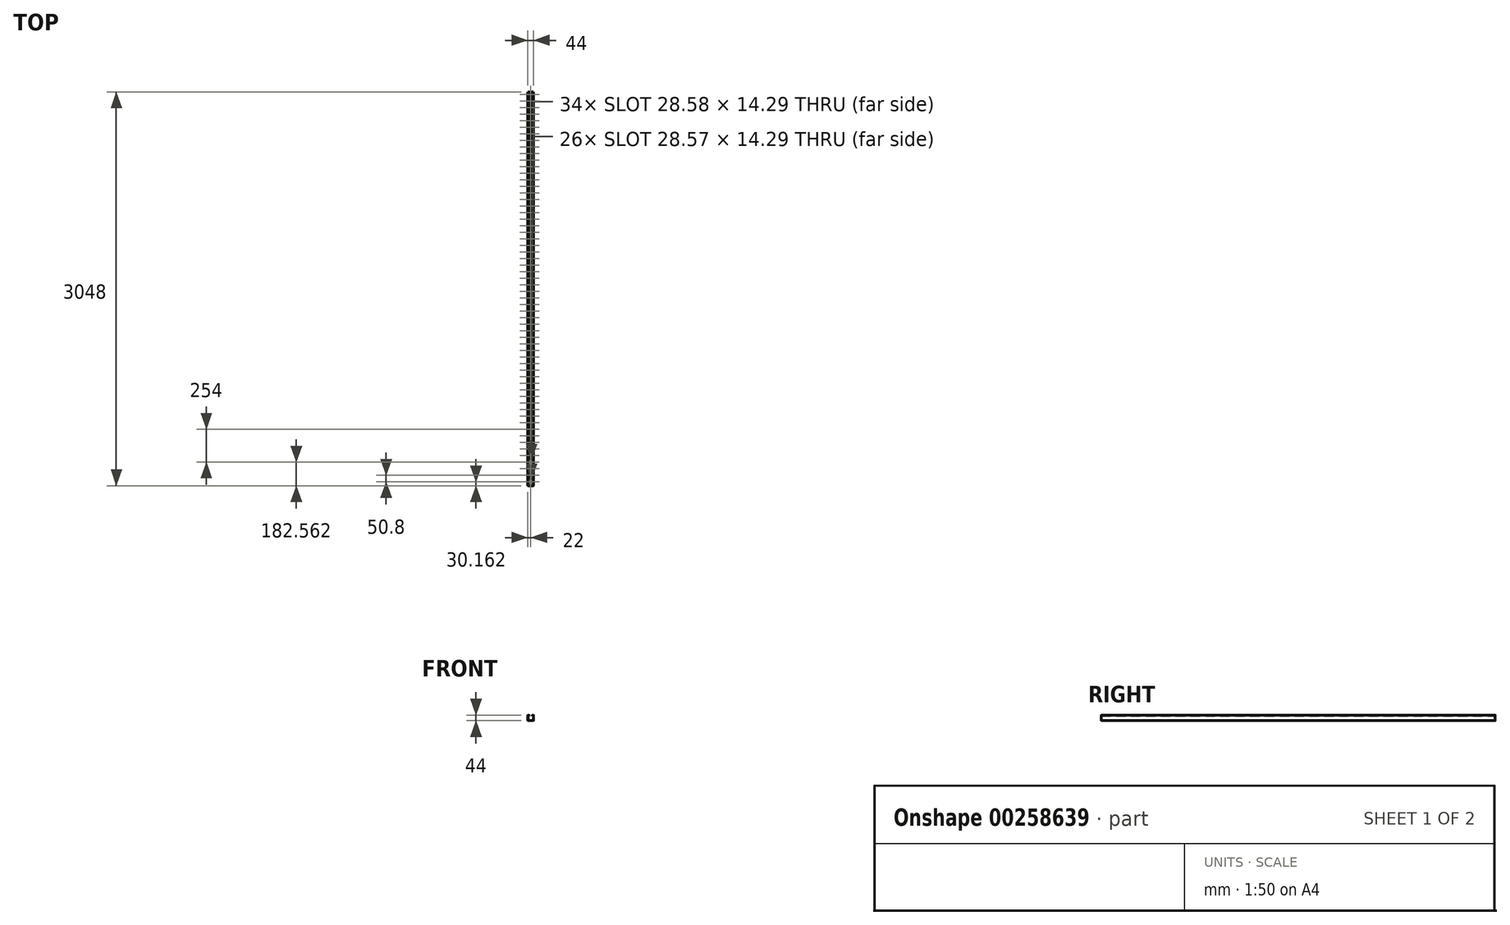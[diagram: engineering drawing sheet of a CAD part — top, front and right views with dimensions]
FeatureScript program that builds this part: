
annotation { "Feature Type Name" : "Feature", "Feature Type Description" : "" }
export const myFeature = defineFeature(function(context is Context, id is Id, definition is map)
    precondition{}
    {
        {
            var Q0;
            Q0=qCreatedBy(makeId("Front.planeOp"),FACE);
            var sketch = newSketch(context, id + "F0", { "sketchPlane" : qUnion([Q0])});
            skLineSegment(sketch, "E0.bottom", {"start": v(-22, 22) * mm, "end": v(22, 22) * mm, "construction": true});
            skLineSegment(sketch, "E0.top", {"start": v(-22, -22) * mm, "end": v(22, -22) * mm, "construction": true});
            skLineSegment(sketch, "E0.left", {"start": v(-22, 22) * mm, "end": v(-22, -22) * mm, "construction": true});
            skLineSegment(sketch, "E0.right", {"start": v(22, 22) * mm, "end": v(22, -22) * mm, "construction": true});
            skPoint(sketch, "E0.middle", {"position": v(0, 0) * mm});
            skLineSegment(sketch, "E1", {"start": v(0, -22) * mm, "end": v(-20.73, -22) * mm});
            skLineSegment(sketch, "E2", {"start": v(-20.73, 22) * mm, "end": v(-13.74, 22) * mm});
            skLineSegment(sketch, "E3", {"start": v(-12.47, 20.73) * mm, "end": v(-12.47, 14.85) * mm});
            skLineSegment(sketch, "E4", {"start": v(-22, -20.73) * mm, "end": v(-22, 20.73) * mm});
            skPoint(sketch, "E5.visualSharp", {"position": v(-22, -22) * mm});
            skArc(sketch, "E5.filletArc", {"start": v(-22, -20.73) * mm, "mid": v(-21.63, -21.63) * mm, "end": v(-20.73, -22) * mm});
            skPoint(sketch, "E6.visualSharp", {"position": v(-22, 22) * mm});
            skArc(sketch, "E6.filletArc", {"start": v(-20.73, 22) * mm, "mid": v(-21.63, 21.63) * mm, "end": v(-22, 20.73) * mm});
            skPoint(sketch, "E7.visualSharp", {"position": v(-12.47, 22) * mm});
            skArc(sketch, "E7.filletArc", {"start": v(-12.47, 20.73) * mm, "mid": v(-12.84, 21.63) * mm, "end": v(-13.74, 22) * mm});
            skLineSegment(sketch, "E8.0", {"start": v(-13.49, 20.73) * mm, "end": v(-13.49, 14.85) * mm});
            skArc(sketch, "E8.1", {"start": v(-13.49, 20.73) * mm, "mid": v(-13.56, 20.9) * mm, "end": v(-13.74, 20.98) * mm});
            skLineSegment(sketch, "E8.2", {"start": v(-20.73, 20.98) * mm, "end": v(-13.74, 20.98) * mm});
            skLineSegment(sketch, "E8.3", {"start": v(0, -20.98) * mm, "end": v(-20.73, -20.98) * mm});
            skArc(sketch, "E8.4", {"start": v(-20.98, -20.73) * mm, "mid": v(-20.9, -20.9) * mm, "end": v(-20.73, -20.98) * mm});
            skLineSegment(sketch, "E8.5", {"start": v(-20.98, -20.73) * mm, "end": v(-20.98, 20.73) * mm});
            skArc(sketch, "E8.6", {"start": v(-20.73, 20.98) * mm, "mid": v(-20.9, 20.9) * mm, "end": v(-20.98, 20.73) * mm});
            skLineSegment(sketch, "E9", {"start": v(-13.49, 14.85) * mm, "end": v(-12.47, 14.85) * mm});
            skLineSegment(sketch, "E10", {"start": v(0, -22) * mm, "end": v(0, -20.98) * mm});
            skSolve(sketch);
        }
        {
            var Q0;
            Q0 = qSketchRegion(id + "F0", true);
            extrude(context, id + "F1", {"entities" : qUnion([Q0]), "endBound" : BoundingType.SYMMETRIC, "depth" : 3048 * mm});
        }
        {
            var Q0;
            Q0=makeQuery(id+"F1.opExtrude","SWEPT_FACE",FACE,{"disambiguationData":[OSD([sQuery(id+"F0.wireOp",EDGE,"E8.3")])]});
            var sketch = newSketch(context, id + "F2", { "sketchPlane" : qUnion([Q0])});
            skLineSegment(sketch, "E11", {"start": v(-20.73, -1493.84) * mm, "end": v(41.03, -1493.84) * mm, "construction": true});
            skLineSegment(sketch, "E12.bottom", {"start": v(-7.14, -1479.55) * mm, "end": v(7.14, -1479.55) * mm, "construction": true});
            skLineSegment(sketch, "E12.top", {"start": v(-7.14, -1508.12) * mm, "end": v(7.14, -1508.12) * mm, "construction": true});
            skLineSegment(sketch, "E12.left", {"start": v(-7.14, -1479.55) * mm, "end": v(-7.14, -1508.12) * mm, "construction": true});
            skLineSegment(sketch, "E12.right", {"start": v(7.14, -1479.55) * mm, "end": v(7.14, -1508.12) * mm, "construction": true});
            skPoint(sketch, "E12.middle", {"position": v(0, -1493.84) * mm});
            skArc(sketch, "E13", {"start": v(0, -1479.55) * mm, "mid": v(-5.05, -1481.64) * mm, "end": v(-7.14, -1486.7) * mm});
            skArc(sketch, "E14", {"start": v(-7.14, -1500.98) * mm, "mid": v(-5.05, -1506.03) * mm, "end": v(0, -1508.12) * mm});
            skLineSegment(sketch, "E15", {"start": v(-7.14, -1486.7) * mm, "end": v(-7.14, -1500.98) * mm});
            skLineSegment(sketch, "E16", {"start": v(0, -1508.12) * mm, "end": v(0, -1479.55) * mm});
            skArc(sketch, "E17.0.1.0", {"start": v(0, -1428.75) * mm, "mid": v(-5.05, -1430.84) * mm, "end": v(-7.14, -1435.9) * mm});
            skLineSegment(sketch, "E17.0.1.1", {"start": v(0, -1457.33) * mm, "end": v(0, -1428.75) * mm});
            skArc(sketch, "E17.0.1.2", {"start": v(-7.14, -1450.18) * mm, "mid": v(-5.05, -1455.23) * mm, "end": v(0, -1457.33) * mm});
            skPoint(sketch, "E17.0.1.3", {"position": v(0, -1443.04) * mm});
            skLineSegment(sketch, "E17.0.1.4", {"start": v(7.14, -1428.75) * mm, "end": v(7.14, -1457.33) * mm, "construction": true});
            skLineSegment(sketch, "E17.0.1.5", {"start": v(-7.14, -1435.9) * mm, "end": v(-7.14, -1450.18) * mm});
            skArc(sketch, "E17.0.2.0", {"start": v(0, -1377.95) * mm, "mid": v(-5.05, -1380.04) * mm, "end": v(-7.14, -1385.1) * mm});
            skLineSegment(sketch, "E17.0.2.1", {"start": v(0, -1406.52) * mm, "end": v(0, -1377.95) * mm});
            skArc(sketch, "E17.0.2.2", {"start": v(-7.14, -1399.38) * mm, "mid": v(-5.05, -1404.43) * mm, "end": v(0, -1406.52) * mm});
            skPoint(sketch, "E17.0.2.3", {"position": v(0, -1392.24) * mm});
            skLineSegment(sketch, "E17.0.2.4", {"start": v(7.14, -1377.95) * mm, "end": v(7.14, -1406.52) * mm, "construction": true});
            skLineSegment(sketch, "E17.0.2.5", {"start": v(-7.14, -1385.1) * mm, "end": v(-7.14, -1399.38) * mm});
            skArc(sketch, "E17.0.3.0", {"start": v(0, -1327.15) * mm, "mid": v(-5.05, -1329.24) * mm, "end": v(-7.14, -1334.3) * mm});
            skLineSegment(sketch, "E17.0.3.1", {"start": v(0, -1355.72) * mm, "end": v(0, -1327.15) * mm});
            skArc(sketch, "E17.0.3.2", {"start": v(-7.14, -1348.58) * mm, "mid": v(-5.05, -1353.63) * mm, "end": v(0, -1355.72) * mm});
            skPoint(sketch, "E17.0.3.3", {"position": v(0, -1341.44) * mm});
            skLineSegment(sketch, "E17.0.3.4", {"start": v(7.14, -1327.15) * mm, "end": v(7.14, -1355.72) * mm, "construction": true});
            skLineSegment(sketch, "E17.0.3.5", {"start": v(-7.14, -1334.3) * mm, "end": v(-7.14, -1348.58) * mm});
            skArc(sketch, "E17.0.4.0", {"start": v(0, -1276.35) * mm, "mid": v(-5.05, -1278.44) * mm, "end": v(-7.14, -1283.5) * mm});
            skLineSegment(sketch, "E17.0.4.1", {"start": v(0, -1304.92) * mm, "end": v(0, -1276.35) * mm});
            skArc(sketch, "E17.0.4.2", {"start": v(-7.14, -1297.78) * mm, "mid": v(-5.05, -1302.83) * mm, "end": v(0, -1304.92) * mm});
            skPoint(sketch, "E17.0.4.3", {"position": v(0, -1290.64) * mm});
            skLineSegment(sketch, "E17.0.4.4", {"start": v(7.14, -1276.35) * mm, "end": v(7.14, -1304.92) * mm, "construction": true});
            skLineSegment(sketch, "E17.0.4.5", {"start": v(-7.14, -1283.5) * mm, "end": v(-7.14, -1297.78) * mm});
            skArc(sketch, "E17.0.5.0", {"start": v(0, -1225.55) * mm, "mid": v(-5.05, -1227.64) * mm, "end": v(-7.14, -1232.7) * mm});
            skLineSegment(sketch, "E17.0.5.1", {"start": v(0, -1254.12) * mm, "end": v(0, -1225.55) * mm});
            skArc(sketch, "E17.0.5.2", {"start": v(-7.14, -1246.98) * mm, "mid": v(-5.05, -1252.03) * mm, "end": v(0, -1254.12) * mm});
            skPoint(sketch, "E17.0.5.3", {"position": v(0, -1239.84) * mm});
            skLineSegment(sketch, "E17.0.5.4", {"start": v(7.14, -1225.55) * mm, "end": v(7.14, -1254.12) * mm, "construction": true});
            skLineSegment(sketch, "E17.0.5.5", {"start": v(-7.14, -1232.7) * mm, "end": v(-7.14, -1246.98) * mm});
            skArc(sketch, "E17.0.6.0", {"start": v(0, -1174.75) * mm, "mid": v(-5.05, -1176.84) * mm, "end": v(-7.14, -1181.9) * mm});
            skLineSegment(sketch, "E17.0.6.1", {"start": v(0, -1203.32) * mm, "end": v(0, -1174.75) * mm});
            skArc(sketch, "E17.0.6.2", {"start": v(-7.14, -1196.18) * mm, "mid": v(-5.05, -1201.23) * mm, "end": v(0, -1203.32) * mm});
            skPoint(sketch, "E17.0.6.3", {"position": v(0, -1189.04) * mm});
            skLineSegment(sketch, "E17.0.6.4", {"start": v(7.14, -1174.75) * mm, "end": v(7.14, -1203.32) * mm, "construction": true});
            skLineSegment(sketch, "E17.0.6.5", {"start": v(-7.14, -1181.9) * mm, "end": v(-7.14, -1196.18) * mm});
            skArc(sketch, "E17.0.7.0", {"start": v(0, -1123.95) * mm, "mid": v(-5.05, -1126.04) * mm, "end": v(-7.14, -1131.1) * mm});
            skLineSegment(sketch, "E17.0.7.1", {"start": v(0, -1152.52) * mm, "end": v(0, -1123.95) * mm});
            skArc(sketch, "E17.0.7.2", {"start": v(-7.14, -1145.38) * mm, "mid": v(-5.05, -1150.43) * mm, "end": v(0, -1152.52) * mm});
            skPoint(sketch, "E17.0.7.3", {"position": v(0, -1138.24) * mm});
            skLineSegment(sketch, "E17.0.7.4", {"start": v(7.14, -1123.95) * mm, "end": v(7.14, -1152.52) * mm, "construction": true});
            skLineSegment(sketch, "E17.0.7.5", {"start": v(-7.14, -1131.1) * mm, "end": v(-7.14, -1145.38) * mm});
            skArc(sketch, "E17.0.8.0", {"start": v(0, -1073.15) * mm, "mid": v(-5.05, -1075.24) * mm, "end": v(-7.14, -1080.3) * mm});
            skLineSegment(sketch, "E17.0.8.1", {"start": v(0, -1101.72) * mm, "end": v(0, -1073.15) * mm});
            skArc(sketch, "E17.0.8.2", {"start": v(-7.14, -1094.58) * mm, "mid": v(-5.05, -1099.63) * mm, "end": v(0, -1101.72) * mm});
            skPoint(sketch, "E17.0.8.3", {"position": v(0, -1087.44) * mm});
            skLineSegment(sketch, "E17.0.8.4", {"start": v(7.14, -1073.15) * mm, "end": v(7.14, -1101.72) * mm, "construction": true});
            skLineSegment(sketch, "E17.0.8.5", {"start": v(-7.14, -1080.3) * mm, "end": v(-7.14, -1094.58) * mm});
            skArc(sketch, "E17.0.9.0", {"start": v(0, -1022.35) * mm, "mid": v(-5.05, -1024.44) * mm, "end": v(-7.14, -1029.5) * mm});
            skLineSegment(sketch, "E17.0.9.1", {"start": v(0, -1050.92) * mm, "end": v(0, -1022.35) * mm});
            skArc(sketch, "E17.0.9.2", {"start": v(-7.14, -1043.78) * mm, "mid": v(-5.05, -1048.83) * mm, "end": v(0, -1050.92) * mm});
            skPoint(sketch, "E17.0.9.3", {"position": v(0, -1036.64) * mm});
            skLineSegment(sketch, "E17.0.9.4", {"start": v(7.14, -1022.35) * mm, "end": v(7.14, -1050.92) * mm, "construction": true});
            skLineSegment(sketch, "E17.0.9.5", {"start": v(-7.14, -1029.5) * mm, "end": v(-7.14, -1043.78) * mm});
            skArc(sketch, "E17.0.10.0", {"start": v(0, -971.55) * mm, "mid": v(-5.05, -973.64) * mm, "end": v(-7.14, -978.7) * mm});
            skLineSegment(sketch, "E17.0.10.1", {"start": v(0, -1000.12) * mm, "end": v(0, -971.55) * mm});
            skArc(sketch, "E17.0.10.2", {"start": v(-7.14, -992.98) * mm, "mid": v(-5.05, -998.03) * mm, "end": v(0, -1000.12) * mm});
            skPoint(sketch, "E17.0.10.3", {"position": v(0, -985.84) * mm});
            skLineSegment(sketch, "E17.0.10.4", {"start": v(7.14, -971.55) * mm, "end": v(7.14, -1000.12) * mm, "construction": true});
            skLineSegment(sketch, "E17.0.10.5", {"start": v(-7.14, -978.7) * mm, "end": v(-7.14, -992.98) * mm});
            skArc(sketch, "E17.0.11.0", {"start": v(0, -920.75) * mm, "mid": v(-5.05, -922.84) * mm, "end": v(-7.14, -927.9) * mm});
            skLineSegment(sketch, "E17.0.11.1", {"start": v(0, -949.32) * mm, "end": v(0, -920.75) * mm});
            skArc(sketch, "E17.0.11.2", {"start": v(-7.14, -942.18) * mm, "mid": v(-5.05, -947.23) * mm, "end": v(0, -949.32) * mm});
            skPoint(sketch, "E17.0.11.3", {"position": v(0, -935.04) * mm});
            skLineSegment(sketch, "E17.0.11.4", {"start": v(7.14, -920.75) * mm, "end": v(7.14, -949.32) * mm, "construction": true});
            skLineSegment(sketch, "E17.0.11.5", {"start": v(-7.14, -927.9) * mm, "end": v(-7.14, -942.18) * mm});
            skArc(sketch, "E17.0.12.0", {"start": v(0, -869.95) * mm, "mid": v(-5.05, -872.04) * mm, "end": v(-7.14, -877.1) * mm});
            skLineSegment(sketch, "E17.0.12.1", {"start": v(0, -898.52) * mm, "end": v(0, -869.95) * mm});
            skArc(sketch, "E17.0.12.2", {"start": v(-7.14, -891.38) * mm, "mid": v(-5.05, -896.43) * mm, "end": v(0, -898.52) * mm});
            skPoint(sketch, "E17.0.12.3", {"position": v(0, -884.24) * mm});
            skLineSegment(sketch, "E17.0.12.4", {"start": v(7.14, -869.95) * mm, "end": v(7.14, -898.52) * mm, "construction": true});
            skLineSegment(sketch, "E17.0.12.5", {"start": v(-7.14, -877.1) * mm, "end": v(-7.14, -891.38) * mm});
            skArc(sketch, "E17.0.13.0", {"start": v(0, -819.15) * mm, "mid": v(-5.05, -821.24) * mm, "end": v(-7.14, -826.3) * mm});
            skLineSegment(sketch, "E17.0.13.1", {"start": v(0, -847.72) * mm, "end": v(0, -819.15) * mm});
            skArc(sketch, "E17.0.13.2", {"start": v(-7.14, -840.58) * mm, "mid": v(-5.05, -845.63) * mm, "end": v(0, -847.72) * mm});
            skPoint(sketch, "E17.0.13.3", {"position": v(0, -833.44) * mm});
            skLineSegment(sketch, "E17.0.13.4", {"start": v(7.14, -819.15) * mm, "end": v(7.14, -847.72) * mm, "construction": true});
            skLineSegment(sketch, "E17.0.13.5", {"start": v(-7.14, -826.3) * mm, "end": v(-7.14, -840.58) * mm});
            skArc(sketch, "E17.0.14.0", {"start": v(0, -768.35) * mm, "mid": v(-5.05, -770.44) * mm, "end": v(-7.14, -775.5) * mm});
            skLineSegment(sketch, "E17.0.14.1", {"start": v(0, -796.92) * mm, "end": v(0, -768.35) * mm});
            skArc(sketch, "E17.0.14.2", {"start": v(-7.14, -789.78) * mm, "mid": v(-5.05, -794.83) * mm, "end": v(0, -796.92) * mm});
            skPoint(sketch, "E17.0.14.3", {"position": v(0, -782.64) * mm});
            skLineSegment(sketch, "E17.0.14.4", {"start": v(7.14, -768.35) * mm, "end": v(7.14, -796.92) * mm, "construction": true});
            skLineSegment(sketch, "E17.0.14.5", {"start": v(-7.14, -775.5) * mm, "end": v(-7.14, -789.78) * mm});
            skArc(sketch, "E17.0.15.0", {"start": v(0, -717.55) * mm, "mid": v(-5.05, -719.64) * mm, "end": v(-7.14, -724.7) * mm});
            skLineSegment(sketch, "E17.0.15.1", {"start": v(0, -746.12) * mm, "end": v(0, -717.55) * mm});
            skArc(sketch, "E17.0.15.2", {"start": v(-7.14, -738.98) * mm, "mid": v(-5.05, -744.03) * mm, "end": v(0, -746.12) * mm});
            skPoint(sketch, "E17.0.15.3", {"position": v(0, -731.84) * mm});
            skLineSegment(sketch, "E17.0.15.4", {"start": v(7.14, -717.55) * mm, "end": v(7.14, -746.12) * mm, "construction": true});
            skLineSegment(sketch, "E17.0.15.5", {"start": v(-7.14, -724.7) * mm, "end": v(-7.14, -738.98) * mm});
            skArc(sketch, "E17.0.16.0", {"start": v(0, -666.75) * mm, "mid": v(-5.05, -668.84) * mm, "end": v(-7.14, -673.9) * mm});
            skLineSegment(sketch, "E17.0.16.1", {"start": v(0, -695.32) * mm, "end": v(0, -666.75) * mm});
            skArc(sketch, "E17.0.16.2", {"start": v(-7.14, -688.18) * mm, "mid": v(-5.05, -693.23) * mm, "end": v(0, -695.32) * mm});
            skPoint(sketch, "E17.0.16.3", {"position": v(0, -681.04) * mm});
            skLineSegment(sketch, "E17.0.16.4", {"start": v(7.14, -666.75) * mm, "end": v(7.14, -695.32) * mm, "construction": true});
            skLineSegment(sketch, "E17.0.16.5", {"start": v(-7.14, -673.9) * mm, "end": v(-7.14, -688.18) * mm});
            skArc(sketch, "E17.0.17.0", {"start": v(0, -615.95) * mm, "mid": v(-5.05, -618.04) * mm, "end": v(-7.14, -623.1) * mm});
            skLineSegment(sketch, "E17.0.17.1", {"start": v(0, -644.52) * mm, "end": v(0, -615.95) * mm});
            skArc(sketch, "E17.0.17.2", {"start": v(-7.14, -637.38) * mm, "mid": v(-5.05, -642.43) * mm, "end": v(0, -644.52) * mm});
            skPoint(sketch, "E17.0.17.3", {"position": v(0, -630.24) * mm});
            skLineSegment(sketch, "E17.0.17.4", {"start": v(7.14, -615.95) * mm, "end": v(7.14, -644.52) * mm, "construction": true});
            skLineSegment(sketch, "E17.0.17.5", {"start": v(-7.14, -623.1) * mm, "end": v(-7.14, -637.38) * mm});
            skArc(sketch, "E17.0.18.0", {"start": v(0, -565.15) * mm, "mid": v(-5.05, -567.24) * mm, "end": v(-7.14, -572.3) * mm});
            skLineSegment(sketch, "E17.0.18.1", {"start": v(0, -593.72) * mm, "end": v(0, -565.15) * mm});
            skArc(sketch, "E17.0.18.2", {"start": v(-7.14, -586.58) * mm, "mid": v(-5.05, -591.63) * mm, "end": v(0, -593.72) * mm});
            skPoint(sketch, "E17.0.18.3", {"position": v(0, -579.44) * mm});
            skLineSegment(sketch, "E17.0.18.4", {"start": v(7.14, -565.15) * mm, "end": v(7.14, -593.72) * mm, "construction": true});
            skLineSegment(sketch, "E17.0.18.5", {"start": v(-7.14, -572.3) * mm, "end": v(-7.14, -586.58) * mm});
            skArc(sketch, "E17.0.19.0", {"start": v(0, -514.35) * mm, "mid": v(-5.05, -516.44) * mm, "end": v(-7.14, -521.5) * mm});
            skLineSegment(sketch, "E17.0.19.1", {"start": v(0, -542.92) * mm, "end": v(0, -514.35) * mm});
            skArc(sketch, "E17.0.19.2", {"start": v(-7.14, -535.78) * mm, "mid": v(-5.05, -540.83) * mm, "end": v(0, -542.92) * mm});
            skPoint(sketch, "E17.0.19.3", {"position": v(0, -528.64) * mm});
            skLineSegment(sketch, "E17.0.19.4", {"start": v(7.14, -514.35) * mm, "end": v(7.14, -542.92) * mm, "construction": true});
            skLineSegment(sketch, "E17.0.19.5", {"start": v(-7.14, -521.5) * mm, "end": v(-7.14, -535.78) * mm});
            skArc(sketch, "E17.0.20.0", {"start": v(0, -463.55) * mm, "mid": v(-5.05, -465.64) * mm, "end": v(-7.14, -470.7) * mm});
            skLineSegment(sketch, "E17.0.20.1", {"start": v(0, -492.12) * mm, "end": v(0, -463.55) * mm});
            skArc(sketch, "E17.0.20.2", {"start": v(-7.14, -484.98) * mm, "mid": v(-5.05, -490.03) * mm, "end": v(0, -492.12) * mm});
            skPoint(sketch, "E17.0.20.3", {"position": v(0, -477.84) * mm});
            skLineSegment(sketch, "E17.0.20.4", {"start": v(7.14, -463.55) * mm, "end": v(7.14, -492.12) * mm, "construction": true});
            skLineSegment(sketch, "E17.0.20.5", {"start": v(-7.14, -470.7) * mm, "end": v(-7.14, -484.98) * mm});
            skArc(sketch, "E17.0.21.0", {"start": v(0, -412.75) * mm, "mid": v(-5.05, -414.84) * mm, "end": v(-7.14, -419.9) * mm});
            skLineSegment(sketch, "E17.0.21.1", {"start": v(0, -441.32) * mm, "end": v(0, -412.75) * mm});
            skArc(sketch, "E17.0.21.2", {"start": v(-7.14, -434.18) * mm, "mid": v(-5.05, -439.23) * mm, "end": v(0, -441.32) * mm});
            skPoint(sketch, "E17.0.21.3", {"position": v(0, -427.04) * mm});
            skLineSegment(sketch, "E17.0.21.4", {"start": v(7.14, -412.75) * mm, "end": v(7.14, -441.32) * mm, "construction": true});
            skLineSegment(sketch, "E17.0.21.5", {"start": v(-7.14, -419.9) * mm, "end": v(-7.14, -434.18) * mm});
            skArc(sketch, "E17.0.22.0", {"start": v(0, -361.95) * mm, "mid": v(-5.05, -364.04) * mm, "end": v(-7.14, -369.1) * mm});
            skLineSegment(sketch, "E17.0.22.1", {"start": v(0, -390.52) * mm, "end": v(0, -361.95) * mm});
            skArc(sketch, "E17.0.22.2", {"start": v(-7.14, -383.38) * mm, "mid": v(-5.05, -388.43) * mm, "end": v(0, -390.52) * mm});
            skPoint(sketch, "E17.0.22.3", {"position": v(0, -376.24) * mm});
            skLineSegment(sketch, "E17.0.22.4", {"start": v(7.14, -361.95) * mm, "end": v(7.14, -390.52) * mm, "construction": true});
            skLineSegment(sketch, "E17.0.22.5", {"start": v(-7.14, -369.1) * mm, "end": v(-7.14, -383.38) * mm});
            skArc(sketch, "E17.0.23.0", {"start": v(0, -311.15) * mm, "mid": v(-5.05, -313.24) * mm, "end": v(-7.14, -318.3) * mm});
            skLineSegment(sketch, "E17.0.23.1", {"start": v(0, -339.72) * mm, "end": v(0, -311.15) * mm});
            skArc(sketch, "E17.0.23.2", {"start": v(-7.14, -332.58) * mm, "mid": v(-5.05, -337.63) * mm, "end": v(0, -339.72) * mm});
            skPoint(sketch, "E17.0.23.3", {"position": v(0, -325.44) * mm});
            skLineSegment(sketch, "E17.0.23.4", {"start": v(7.14, -311.15) * mm, "end": v(7.14, -339.72) * mm, "construction": true});
            skLineSegment(sketch, "E17.0.23.5", {"start": v(-7.14, -318.3) * mm, "end": v(-7.14, -332.58) * mm});
            skArc(sketch, "E17.0.24.0", {"start": v(0, -260.35) * mm, "mid": v(-5.05, -262.44) * mm, "end": v(-7.14, -267.5) * mm});
            skLineSegment(sketch, "E17.0.24.1", {"start": v(0, -288.92) * mm, "end": v(0, -260.35) * mm});
            skArc(sketch, "E17.0.24.2", {"start": v(-7.14, -281.78) * mm, "mid": v(-5.05, -286.83) * mm, "end": v(0, -288.92) * mm});
            skPoint(sketch, "E17.0.24.3", {"position": v(0, -274.64) * mm});
            skLineSegment(sketch, "E17.0.24.4", {"start": v(7.14, -260.35) * mm, "end": v(7.14, -288.92) * mm, "construction": true});
            skLineSegment(sketch, "E17.0.24.5", {"start": v(-7.14, -267.5) * mm, "end": v(-7.14, -281.78) * mm});
            skLineSegment(sketch, "E17.direction1", {"start": v(0, -1508.12) * mm, "end": v(25.4, -1508.12) * mm, "construction": true});
            skLineSegment(sketch, "E17.direction2", {"start": v(0, -1508.12) * mm, "end": v(0, -1457.33) * mm, "construction": true});
            skArc(sketch, "E18.0.0.25", {"start": v(0, -209.55) * mm, "mid": v(-5.05, -211.64) * mm, "end": v(-7.14, -216.7) * mm});
            skLineSegment(sketch, "E18.4.0.25", {"start": v(0, -238.12) * mm, "end": v(0, -209.55) * mm});
            skArc(sketch, "E18.7.0.25", {"start": v(-7.14, -230.98) * mm, "mid": v(-5.05, -236.03) * mm, "end": v(0, -238.12) * mm});
            skPoint(sketch, "E18.11.0.25", {"position": v(0, -223.84) * mm});
            skLineSegment(sketch, "E18.12.0.25", {"start": v(7.14, -209.55) * mm, "end": v(7.14, -238.12) * mm, "construction": true});
            skLineSegment(sketch, "E18.15.0.25", {"start": v(-7.14, -216.7) * mm, "end": v(-7.14, -230.98) * mm});
            skArc(sketch, "E18.0.0.26", {"start": v(0, -158.75) * mm, "mid": v(-5.05, -160.84) * mm, "end": v(-7.14, -165.9) * mm});
            skLineSegment(sketch, "E18.4.0.26", {"start": v(0, -187.32) * mm, "end": v(0, -158.75) * mm});
            skArc(sketch, "E18.7.0.26", {"start": v(-7.14, -180.18) * mm, "mid": v(-5.05, -185.23) * mm, "end": v(0, -187.32) * mm});
            skPoint(sketch, "E18.11.0.26", {"position": v(0, -173.04) * mm});
            skLineSegment(sketch, "E18.12.0.26", {"start": v(7.14, -158.75) * mm, "end": v(7.14, -187.32) * mm, "construction": true});
            skLineSegment(sketch, "E18.15.0.26", {"start": v(-7.14, -165.9) * mm, "end": v(-7.14, -180.18) * mm});
            skArc(sketch, "E18.0.0.27", {"start": v(0, -107.95) * mm, "mid": v(-5.05, -110.04) * mm, "end": v(-7.14, -115.1) * mm});
            skLineSegment(sketch, "E18.4.0.27", {"start": v(0, -136.52) * mm, "end": v(0, -107.95) * mm});
            skArc(sketch, "E18.7.0.27", {"start": v(-7.14, -129.38) * mm, "mid": v(-5.05, -134.43) * mm, "end": v(0, -136.52) * mm});
            skPoint(sketch, "E18.11.0.27", {"position": v(0, -122.24) * mm});
            skLineSegment(sketch, "E18.12.0.27", {"start": v(7.14, -107.95) * mm, "end": v(7.14, -136.52) * mm, "construction": true});
            skLineSegment(sketch, "E18.15.0.27", {"start": v(-7.14, -115.1) * mm, "end": v(-7.14, -129.38) * mm});
            skArc(sketch, "E18.0.0.28", {"start": v(0, -57.15) * mm, "mid": v(-5.05, -59.24) * mm, "end": v(-7.14, -64.3) * mm});
            skLineSegment(sketch, "E18.4.0.28", {"start": v(0, -85.72) * mm, "end": v(0, -57.15) * mm});
            skArc(sketch, "E18.7.0.28", {"start": v(-7.14, -78.58) * mm, "mid": v(-5.05, -83.63) * mm, "end": v(0, -85.72) * mm});
            skPoint(sketch, "E18.11.0.28", {"position": v(0, -71.44) * mm});
            skLineSegment(sketch, "E18.12.0.28", {"start": v(7.14, -57.15) * mm, "end": v(7.14, -85.72) * mm, "construction": true});
            skLineSegment(sketch, "E18.15.0.28", {"start": v(-7.14, -64.3) * mm, "end": v(-7.14, -78.58) * mm});
            skArc(sketch, "E18.0.0.29", {"start": v(0, -6.35) * mm, "mid": v(-5.05, -8.44) * mm, "end": v(-7.14, -13.5) * mm});
            skLineSegment(sketch, "E18.4.0.29", {"start": v(0, -34.92) * mm, "end": v(0, -6.35) * mm});
            skArc(sketch, "E18.7.0.29", {"start": v(-7.14, -27.78) * mm, "mid": v(-5.05, -32.83) * mm, "end": v(0, -34.92) * mm});
            skPoint(sketch, "E18.11.0.29", {"position": v(0, -20.64) * mm});
            skLineSegment(sketch, "E18.12.0.29", {"start": v(7.14, -6.35) * mm, "end": v(7.14, -34.92) * mm, "construction": true});
            skLineSegment(sketch, "E18.15.0.29", {"start": v(-7.14, -13.5) * mm, "end": v(-7.14, -27.78) * mm});
            skArc(sketch, "E18.0.0.30", {"start": v(0, 44.45) * mm, "mid": v(-5.05, 42.36) * mm, "end": v(-7.14, 37.3) * mm});
            skLineSegment(sketch, "E18.4.0.30", {"start": v(0, 15.88) * mm, "end": v(0, 44.45) * mm});
            skArc(sketch, "E18.7.0.30", {"start": v(-7.14, 23.02) * mm, "mid": v(-5.05, 17.97) * mm, "end": v(0, 15.88) * mm});
            skPoint(sketch, "E18.11.0.30", {"position": v(0, 30.16) * mm});
            skLineSegment(sketch, "E18.12.0.30", {"start": v(7.14, 44.45) * mm, "end": v(7.14, 15.88) * mm, "construction": true});
            skLineSegment(sketch, "E18.15.0.30", {"start": v(-7.14, 37.3) * mm, "end": v(-7.14, 23.02) * mm});
            skArc(sketch, "E18.0.0.31", {"start": v(0, 95.25) * mm, "mid": v(-5.05, 93.16) * mm, "end": v(-7.14, 88.1) * mm});
            skLineSegment(sketch, "E18.4.0.31", {"start": v(0, 66.68) * mm, "end": v(0, 95.25) * mm});
            skArc(sketch, "E18.7.0.31", {"start": v(-7.14, 73.82) * mm, "mid": v(-5.05, 68.77) * mm, "end": v(0, 66.68) * mm});
            skPoint(sketch, "E18.11.0.31", {"position": v(0, 80.96) * mm});
            skLineSegment(sketch, "E18.12.0.31", {"start": v(7.14, 95.25) * mm, "end": v(7.14, 66.68) * mm, "construction": true});
            skLineSegment(sketch, "E18.15.0.31", {"start": v(-7.14, 88.1) * mm, "end": v(-7.14, 73.82) * mm});
            skArc(sketch, "E18.0.0.32", {"start": v(0, 146.05) * mm, "mid": v(-5.05, 143.96) * mm, "end": v(-7.14, 138.9) * mm});
            skLineSegment(sketch, "E18.4.0.32", {"start": v(0, 117.48) * mm, "end": v(0, 146.05) * mm});
            skArc(sketch, "E18.7.0.32", {"start": v(-7.14, 124.62) * mm, "mid": v(-5.05, 119.57) * mm, "end": v(0, 117.48) * mm});
            skPoint(sketch, "E18.11.0.32", {"position": v(0, 131.76) * mm});
            skLineSegment(sketch, "E18.12.0.32", {"start": v(7.14, 146.05) * mm, "end": v(7.14, 117.48) * mm, "construction": true});
            skLineSegment(sketch, "E18.15.0.32", {"start": v(-7.14, 138.9) * mm, "end": v(-7.14, 124.62) * mm});
            skArc(sketch, "E18.0.0.33", {"start": v(0, 196.85) * mm, "mid": v(-5.05, 194.76) * mm, "end": v(-7.14, 189.7) * mm});
            skLineSegment(sketch, "E18.4.0.33", {"start": v(0, 168.28) * mm, "end": v(0, 196.85) * mm});
            skArc(sketch, "E18.7.0.33", {"start": v(-7.14, 175.42) * mm, "mid": v(-5.05, 170.37) * mm, "end": v(0, 168.28) * mm});
            skPoint(sketch, "E18.11.0.33", {"position": v(0, 182.56) * mm});
            skLineSegment(sketch, "E18.12.0.33", {"start": v(7.14, 196.85) * mm, "end": v(7.14, 168.28) * mm, "construction": true});
            skLineSegment(sketch, "E18.15.0.33", {"start": v(-7.14, 189.7) * mm, "end": v(-7.14, 175.42) * mm});
            skArc(sketch, "E18.0.0.34", {"start": v(0, 247.65) * mm, "mid": v(-5.05, 245.56) * mm, "end": v(-7.14, 240.5) * mm});
            skLineSegment(sketch, "E18.4.0.34", {"start": v(0, 219.08) * mm, "end": v(0, 247.65) * mm});
            skArc(sketch, "E18.7.0.34", {"start": v(-7.14, 226.22) * mm, "mid": v(-5.05, 221.17) * mm, "end": v(0, 219.08) * mm});
            skPoint(sketch, "E18.11.0.34", {"position": v(0, 233.36) * mm});
            skLineSegment(sketch, "E18.12.0.34", {"start": v(7.14, 247.65) * mm, "end": v(7.14, 219.08) * mm, "construction": true});
            skLineSegment(sketch, "E18.15.0.34", {"start": v(-7.14, 240.5) * mm, "end": v(-7.14, 226.22) * mm});
            skArc(sketch, "E18.0.0.35", {"start": v(0, 298.45) * mm, "mid": v(-5.05, 296.36) * mm, "end": v(-7.14, 291.3) * mm});
            skLineSegment(sketch, "E18.4.0.35", {"start": v(0, 269.88) * mm, "end": v(0, 298.45) * mm});
            skArc(sketch, "E18.7.0.35", {"start": v(-7.14, 277.02) * mm, "mid": v(-5.05, 271.97) * mm, "end": v(0, 269.88) * mm});
            skPoint(sketch, "E18.11.0.35", {"position": v(0, 284.16) * mm});
            skLineSegment(sketch, "E18.12.0.35", {"start": v(7.14, 298.45) * mm, "end": v(7.14, 269.88) * mm, "construction": true});
            skLineSegment(sketch, "E18.15.0.35", {"start": v(-7.14, 291.3) * mm, "end": v(-7.14, 277.02) * mm});
            skArc(sketch, "E18.0.0.36", {"start": v(0, 349.25) * mm, "mid": v(-5.05, 347.16) * mm, "end": v(-7.14, 342.1) * mm});
            skLineSegment(sketch, "E18.4.0.36", {"start": v(0, 320.68) * mm, "end": v(0, 349.25) * mm});
            skArc(sketch, "E18.7.0.36", {"start": v(-7.14, 327.82) * mm, "mid": v(-5.05, 322.77) * mm, "end": v(0, 320.68) * mm});
            skPoint(sketch, "E18.11.0.36", {"position": v(0, 334.96) * mm});
            skLineSegment(sketch, "E18.12.0.36", {"start": v(7.14, 349.25) * mm, "end": v(7.14, 320.68) * mm, "construction": true});
            skLineSegment(sketch, "E18.15.0.36", {"start": v(-7.14, 342.1) * mm, "end": v(-7.14, 327.82) * mm});
            skArc(sketch, "E18.0.0.37", {"start": v(0, 400.05) * mm, "mid": v(-5.05, 397.96) * mm, "end": v(-7.14, 392.9) * mm});
            skLineSegment(sketch, "E18.4.0.37", {"start": v(0, 371.48) * mm, "end": v(0, 400.05) * mm});
            skArc(sketch, "E18.7.0.37", {"start": v(-7.14, 378.62) * mm, "mid": v(-5.05, 373.57) * mm, "end": v(0, 371.48) * mm});
            skPoint(sketch, "E18.11.0.37", {"position": v(0, 385.76) * mm});
            skLineSegment(sketch, "E18.12.0.37", {"start": v(7.14, 400.05) * mm, "end": v(7.14, 371.48) * mm, "construction": true});
            skLineSegment(sketch, "E18.15.0.37", {"start": v(-7.14, 392.9) * mm, "end": v(-7.14, 378.62) * mm});
            skArc(sketch, "E18.0.0.38", {"start": v(0, 450.85) * mm, "mid": v(-5.05, 448.76) * mm, "end": v(-7.14, 443.7) * mm});
            skLineSegment(sketch, "E18.4.0.38", {"start": v(0, 422.28) * mm, "end": v(0, 450.85) * mm});
            skArc(sketch, "E18.7.0.38", {"start": v(-7.14, 429.42) * mm, "mid": v(-5.05, 424.37) * mm, "end": v(0, 422.28) * mm});
            skPoint(sketch, "E18.11.0.38", {"position": v(0, 436.56) * mm});
            skLineSegment(sketch, "E18.12.0.38", {"start": v(7.14, 450.85) * mm, "end": v(7.14, 422.28) * mm, "construction": true});
            skLineSegment(sketch, "E18.15.0.38", {"start": v(-7.14, 443.7) * mm, "end": v(-7.14, 429.42) * mm});
            skArc(sketch, "E18.0.0.39", {"start": v(0, 501.65) * mm, "mid": v(-5.05, 499.56) * mm, "end": v(-7.14, 494.5) * mm});
            skLineSegment(sketch, "E18.4.0.39", {"start": v(0, 473.08) * mm, "end": v(0, 501.65) * mm});
            skArc(sketch, "E18.7.0.39", {"start": v(-7.14, 480.22) * mm, "mid": v(-5.05, 475.17) * mm, "end": v(0, 473.08) * mm});
            skPoint(sketch, "E18.11.0.39", {"position": v(0, 487.36) * mm});
            skLineSegment(sketch, "E18.12.0.39", {"start": v(7.14, 501.65) * mm, "end": v(7.14, 473.08) * mm, "construction": true});
            skLineSegment(sketch, "E18.15.0.39", {"start": v(-7.14, 494.5) * mm, "end": v(-7.14, 480.22) * mm});
            skArc(sketch, "E18.0.0.40", {"start": v(0, 552.45) * mm, "mid": v(-5.05, 550.36) * mm, "end": v(-7.14, 545.3) * mm});
            skLineSegment(sketch, "E18.4.0.40", {"start": v(0, 523.88) * mm, "end": v(0, 552.45) * mm});
            skArc(sketch, "E18.7.0.40", {"start": v(-7.14, 531.02) * mm, "mid": v(-5.05, 525.97) * mm, "end": v(0, 523.88) * mm});
            skPoint(sketch, "E18.11.0.40", {"position": v(0, 538.16) * mm});
            skLineSegment(sketch, "E18.12.0.40", {"start": v(7.14, 552.45) * mm, "end": v(7.14, 523.88) * mm, "construction": true});
            skLineSegment(sketch, "E18.15.0.40", {"start": v(-7.14, 545.3) * mm, "end": v(-7.14, 531.02) * mm});
            skArc(sketch, "E18.0.0.41", {"start": v(0, 603.25) * mm, "mid": v(-5.05, 601.16) * mm, "end": v(-7.14, 596.1) * mm});
            skLineSegment(sketch, "E18.4.0.41", {"start": v(0, 574.68) * mm, "end": v(0, 603.25) * mm});
            skArc(sketch, "E18.7.0.41", {"start": v(-7.14, 581.82) * mm, "mid": v(-5.05, 576.77) * mm, "end": v(0, 574.68) * mm});
            skPoint(sketch, "E18.11.0.41", {"position": v(0, 588.96) * mm});
            skLineSegment(sketch, "E18.12.0.41", {"start": v(7.14, 603.25) * mm, "end": v(7.14, 574.68) * mm, "construction": true});
            skLineSegment(sketch, "E18.15.0.41", {"start": v(-7.14, 596.1) * mm, "end": v(-7.14, 581.82) * mm});
            skArc(sketch, "E18.0.0.42", {"start": v(0, 654.05) * mm, "mid": v(-5.05, 651.96) * mm, "end": v(-7.14, 646.9) * mm});
            skLineSegment(sketch, "E18.4.0.42", {"start": v(0, 625.48) * mm, "end": v(0, 654.05) * mm});
            skArc(sketch, "E18.7.0.42", {"start": v(-7.14, 632.62) * mm, "mid": v(-5.05, 627.57) * mm, "end": v(0, 625.48) * mm});
            skPoint(sketch, "E18.11.0.42", {"position": v(0, 639.76) * mm});
            skLineSegment(sketch, "E18.12.0.42", {"start": v(7.14, 654.05) * mm, "end": v(7.14, 625.48) * mm, "construction": true});
            skLineSegment(sketch, "E18.15.0.42", {"start": v(-7.14, 646.9) * mm, "end": v(-7.14, 632.62) * mm});
            skArc(sketch, "E18.0.0.43", {"start": v(0, 704.85) * mm, "mid": v(-5.05, 702.76) * mm, "end": v(-7.14, 697.7) * mm});
            skLineSegment(sketch, "E18.4.0.43", {"start": v(0, 676.28) * mm, "end": v(0, 704.85) * mm});
            skArc(sketch, "E18.7.0.43", {"start": v(-7.14, 683.42) * mm, "mid": v(-5.05, 678.37) * mm, "end": v(0, 676.28) * mm});
            skPoint(sketch, "E18.11.0.43", {"position": v(0, 690.56) * mm});
            skLineSegment(sketch, "E18.12.0.43", {"start": v(7.14, 704.85) * mm, "end": v(7.14, 676.28) * mm, "construction": true});
            skLineSegment(sketch, "E18.15.0.43", {"start": v(-7.14, 697.7) * mm, "end": v(-7.14, 683.42) * mm});
            skArc(sketch, "E18.0.0.44", {"start": v(0, 755.65) * mm, "mid": v(-5.05, 753.56) * mm, "end": v(-7.14, 748.5) * mm});
            skLineSegment(sketch, "E18.4.0.44", {"start": v(0, 727.08) * mm, "end": v(0, 755.65) * mm});
            skArc(sketch, "E18.7.0.44", {"start": v(-7.14, 734.22) * mm, "mid": v(-5.05, 729.17) * mm, "end": v(0, 727.08) * mm});
            skPoint(sketch, "E18.11.0.44", {"position": v(0, 741.36) * mm});
            skLineSegment(sketch, "E18.12.0.44", {"start": v(7.14, 755.65) * mm, "end": v(7.14, 727.08) * mm, "construction": true});
            skLineSegment(sketch, "E18.15.0.44", {"start": v(-7.14, 748.5) * mm, "end": v(-7.14, 734.22) * mm});
            skArc(sketch, "E18.0.0.45", {"start": v(0, 806.45) * mm, "mid": v(-5.05, 804.36) * mm, "end": v(-7.14, 799.3) * mm});
            skLineSegment(sketch, "E18.4.0.45", {"start": v(0, 777.88) * mm, "end": v(0, 806.45) * mm});
            skArc(sketch, "E18.7.0.45", {"start": v(-7.14, 785.02) * mm, "mid": v(-5.05, 779.97) * mm, "end": v(0, 777.88) * mm});
            skPoint(sketch, "E18.11.0.45", {"position": v(0, 792.16) * mm});
            skLineSegment(sketch, "E18.12.0.45", {"start": v(7.14, 806.45) * mm, "end": v(7.14, 777.88) * mm, "construction": true});
            skLineSegment(sketch, "E18.15.0.45", {"start": v(-7.14, 799.3) * mm, "end": v(-7.14, 785.02) * mm});
            skArc(sketch, "E18.0.0.46", {"start": v(0, 857.25) * mm, "mid": v(-5.05, 855.16) * mm, "end": v(-7.14, 850.1) * mm});
            skLineSegment(sketch, "E18.4.0.46", {"start": v(0, 828.68) * mm, "end": v(0, 857.25) * mm});
            skArc(sketch, "E18.7.0.46", {"start": v(-7.14, 835.82) * mm, "mid": v(-5.05, 830.77) * mm, "end": v(0, 828.68) * mm});
            skPoint(sketch, "E18.11.0.46", {"position": v(0, 842.96) * mm});
            skLineSegment(sketch, "E18.12.0.46", {"start": v(7.14, 857.25) * mm, "end": v(7.14, 828.68) * mm, "construction": true});
            skLineSegment(sketch, "E18.15.0.46", {"start": v(-7.14, 850.1) * mm, "end": v(-7.14, 835.82) * mm});
            skArc(sketch, "E18.0.0.47", {"start": v(0, 908.05) * mm, "mid": v(-5.05, 905.96) * mm, "end": v(-7.14, 900.9) * mm});
            skLineSegment(sketch, "E18.4.0.47", {"start": v(0, 879.48) * mm, "end": v(0, 908.05) * mm});
            skArc(sketch, "E18.7.0.47", {"start": v(-7.14, 886.62) * mm, "mid": v(-5.05, 881.57) * mm, "end": v(0, 879.48) * mm});
            skPoint(sketch, "E18.11.0.47", {"position": v(0, 893.76) * mm});
            skLineSegment(sketch, "E18.12.0.47", {"start": v(7.14, 908.05) * mm, "end": v(7.14, 879.48) * mm, "construction": true});
            skLineSegment(sketch, "E18.15.0.47", {"start": v(-7.14, 900.9) * mm, "end": v(-7.14, 886.62) * mm});
            skArc(sketch, "E18.0.0.48", {"start": v(0, 958.85) * mm, "mid": v(-5.05, 956.76) * mm, "end": v(-7.14, 951.7) * mm});
            skLineSegment(sketch, "E18.4.0.48", {"start": v(0, 930.28) * mm, "end": v(0, 958.85) * mm});
            skArc(sketch, "E18.7.0.48", {"start": v(-7.14, 937.42) * mm, "mid": v(-5.05, 932.37) * mm, "end": v(0, 930.28) * mm});
            skPoint(sketch, "E18.11.0.48", {"position": v(0, 944.56) * mm});
            skLineSegment(sketch, "E18.12.0.48", {"start": v(7.14, 958.85) * mm, "end": v(7.14, 930.28) * mm, "construction": true});
            skLineSegment(sketch, "E18.15.0.48", {"start": v(-7.14, 951.7) * mm, "end": v(-7.14, 937.42) * mm});
            skArc(sketch, "E18.0.0.49", {"start": v(0, 1009.65) * mm, "mid": v(-5.05, 1007.56) * mm, "end": v(-7.14, 1002.5) * mm});
            skLineSegment(sketch, "E18.4.0.49", {"start": v(0, 981.08) * mm, "end": v(0, 1009.65) * mm});
            skArc(sketch, "E18.7.0.49", {"start": v(-7.14, 988.22) * mm, "mid": v(-5.05, 983.17) * mm, "end": v(0, 981.08) * mm});
            skPoint(sketch, "E18.11.0.49", {"position": v(0, 995.36) * mm});
            skLineSegment(sketch, "E18.12.0.49", {"start": v(7.14, 1009.65) * mm, "end": v(7.14, 981.08) * mm, "construction": true});
            skLineSegment(sketch, "E18.15.0.49", {"start": v(-7.14, 1002.5) * mm, "end": v(-7.14, 988.22) * mm});
            skArc(sketch, "E18.0.0.50", {"start": v(0, 1060.45) * mm, "mid": v(-5.05, 1058.36) * mm, "end": v(-7.14, 1053.3) * mm});
            skLineSegment(sketch, "E18.4.0.50", {"start": v(0, 1031.88) * mm, "end": v(0, 1060.45) * mm});
            skArc(sketch, "E18.7.0.50", {"start": v(-7.14, 1039.02) * mm, "mid": v(-5.05, 1033.97) * mm, "end": v(0, 1031.88) * mm});
            skPoint(sketch, "E18.11.0.50", {"position": v(0, 1046.16) * mm});
            skLineSegment(sketch, "E18.12.0.50", {"start": v(7.14, 1060.45) * mm, "end": v(7.14, 1031.88) * mm, "construction": true});
            skLineSegment(sketch, "E18.15.0.50", {"start": v(-7.14, 1053.3) * mm, "end": v(-7.14, 1039.02) * mm});
            skArc(sketch, "E19.0.0.51", {"start": v(0, 1111.25) * mm, "mid": v(-5.05, 1109.16) * mm, "end": v(-7.14, 1104.1) * mm});
            skLineSegment(sketch, "E19.4.0.51", {"start": v(0, 1082.68) * mm, "end": v(0, 1111.25) * mm});
            skArc(sketch, "E19.7.0.51", {"start": v(-7.14, 1089.82) * mm, "mid": v(-5.05, 1084.77) * mm, "end": v(0, 1082.68) * mm});
            skPoint(sketch, "E19.11.0.51", {"position": v(0, 1096.96) * mm});
            skLineSegment(sketch, "E19.12.0.51", {"start": v(7.14, 1111.25) * mm, "end": v(7.14, 1082.68) * mm, "construction": true});
            skLineSegment(sketch, "E19.15.0.51", {"start": v(-7.14, 1104.1) * mm, "end": v(-7.14, 1089.82) * mm});
            skArc(sketch, "E19.0.0.52", {"start": v(0, 1162.05) * mm, "mid": v(-5.05, 1159.96) * mm, "end": v(-7.14, 1154.9) * mm});
            skLineSegment(sketch, "E19.4.0.52", {"start": v(0, 1133.48) * mm, "end": v(0, 1162.05) * mm});
            skArc(sketch, "E19.7.0.52", {"start": v(-7.14, 1140.62) * mm, "mid": v(-5.05, 1135.57) * mm, "end": v(0, 1133.48) * mm});
            skPoint(sketch, "E19.11.0.52", {"position": v(0, 1147.76) * mm});
            skLineSegment(sketch, "E19.12.0.52", {"start": v(7.14, 1162.05) * mm, "end": v(7.14, 1133.48) * mm, "construction": true});
            skLineSegment(sketch, "E19.15.0.52", {"start": v(-7.14, 1154.9) * mm, "end": v(-7.14, 1140.62) * mm});
            skArc(sketch, "E19.0.0.53", {"start": v(0, 1212.85) * mm, "mid": v(-5.05, 1210.76) * mm, "end": v(-7.14, 1205.7) * mm});
            skLineSegment(sketch, "E19.4.0.53", {"start": v(0, 1184.28) * mm, "end": v(0, 1212.85) * mm});
            skArc(sketch, "E19.7.0.53", {"start": v(-7.14, 1191.42) * mm, "mid": v(-5.05, 1186.37) * mm, "end": v(0, 1184.28) * mm});
            skPoint(sketch, "E19.11.0.53", {"position": v(0, 1198.56) * mm});
            skLineSegment(sketch, "E19.12.0.53", {"start": v(7.14, 1212.85) * mm, "end": v(7.14, 1184.28) * mm, "construction": true});
            skLineSegment(sketch, "E19.15.0.53", {"start": v(-7.14, 1205.7) * mm, "end": v(-7.14, 1191.42) * mm});
            skArc(sketch, "E19.0.0.54", {"start": v(0, 1263.65) * mm, "mid": v(-5.05, 1261.56) * mm, "end": v(-7.14, 1256.5) * mm});
            skLineSegment(sketch, "E19.4.0.54", {"start": v(0, 1235.08) * mm, "end": v(0, 1263.65) * mm});
            skArc(sketch, "E19.7.0.54", {"start": v(-7.14, 1242.22) * mm, "mid": v(-5.05, 1237.17) * mm, "end": v(0, 1235.08) * mm});
            skPoint(sketch, "E19.11.0.54", {"position": v(0, 1249.36) * mm});
            skLineSegment(sketch, "E19.12.0.54", {"start": v(7.14, 1263.65) * mm, "end": v(7.14, 1235.08) * mm, "construction": true});
            skLineSegment(sketch, "E19.15.0.54", {"start": v(-7.14, 1256.5) * mm, "end": v(-7.14, 1242.22) * mm});
            skArc(sketch, "E19.0.0.55", {"start": v(0, 1314.45) * mm, "mid": v(-5.05, 1312.36) * mm, "end": v(-7.14, 1307.3) * mm});
            skLineSegment(sketch, "E19.4.0.55", {"start": v(0, 1285.88) * mm, "end": v(0, 1314.45) * mm});
            skArc(sketch, "E19.7.0.55", {"start": v(-7.14, 1293.02) * mm, "mid": v(-5.05, 1287.97) * mm, "end": v(0, 1285.88) * mm});
            skPoint(sketch, "E19.11.0.55", {"position": v(0, 1300.16) * mm});
            skLineSegment(sketch, "E19.12.0.55", {"start": v(7.14, 1314.45) * mm, "end": v(7.14, 1285.88) * mm, "construction": true});
            skLineSegment(sketch, "E19.15.0.55", {"start": v(-7.14, 1307.3) * mm, "end": v(-7.14, 1293.02) * mm});
            skArc(sketch, "E19.0.0.56", {"start": v(0, 1365.25) * mm, "mid": v(-5.05, 1363.16) * mm, "end": v(-7.14, 1358.1) * mm});
            skLineSegment(sketch, "E19.4.0.56", {"start": v(0, 1336.68) * mm, "end": v(0, 1365.25) * mm});
            skArc(sketch, "E19.7.0.56", {"start": v(-7.14, 1343.82) * mm, "mid": v(-5.05, 1338.77) * mm, "end": v(0, 1336.68) * mm});
            skPoint(sketch, "E19.11.0.56", {"position": v(0, 1350.96) * mm});
            skLineSegment(sketch, "E19.12.0.56", {"start": v(7.14, 1365.25) * mm, "end": v(7.14, 1336.68) * mm, "construction": true});
            skLineSegment(sketch, "E19.15.0.56", {"start": v(-7.14, 1358.1) * mm, "end": v(-7.14, 1343.82) * mm});
            skArc(sketch, "E19.0.0.57", {"start": v(0, 1416.05) * mm, "mid": v(-5.05, 1413.96) * mm, "end": v(-7.14, 1408.9) * mm});
            skLineSegment(sketch, "E19.4.0.57", {"start": v(0, 1387.48) * mm, "end": v(0, 1416.05) * mm});
            skArc(sketch, "E19.7.0.57", {"start": v(-7.14, 1394.62) * mm, "mid": v(-5.05, 1389.57) * mm, "end": v(0, 1387.48) * mm});
            skPoint(sketch, "E19.11.0.57", {"position": v(0, 1401.76) * mm});
            skLineSegment(sketch, "E19.12.0.57", {"start": v(7.14, 1416.05) * mm, "end": v(7.14, 1387.48) * mm, "construction": true});
            skLineSegment(sketch, "E19.15.0.57", {"start": v(-7.14, 1408.9) * mm, "end": v(-7.14, 1394.62) * mm});
            skArc(sketch, "E19.0.0.58", {"start": v(0, 1466.85) * mm, "mid": v(-5.05, 1464.76) * mm, "end": v(-7.14, 1459.7) * mm});
            skLineSegment(sketch, "E19.4.0.58", {"start": v(0, 1438.28) * mm, "end": v(0, 1466.85) * mm});
            skArc(sketch, "E19.7.0.58", {"start": v(-7.14, 1445.42) * mm, "mid": v(-5.05, 1440.37) * mm, "end": v(0, 1438.28) * mm});
            skPoint(sketch, "E19.11.0.58", {"position": v(0, 1452.56) * mm});
            skLineSegment(sketch, "E19.12.0.58", {"start": v(7.14, 1466.85) * mm, "end": v(7.14, 1438.28) * mm, "construction": true});
            skLineSegment(sketch, "E19.15.0.58", {"start": v(-7.14, 1459.7) * mm, "end": v(-7.14, 1445.42) * mm});
            skArc(sketch, "E20.0.0.59", {"start": v(0, 1517.65) * mm, "mid": v(-5.05, 1515.56) * mm, "end": v(-7.14, 1510.5) * mm});
            skLineSegment(sketch, "E20.4.0.59", {"start": v(0, 1489.08) * mm, "end": v(0, 1517.65) * mm});
            skArc(sketch, "E20.7.0.59", {"start": v(-7.14, 1496.22) * mm, "mid": v(-5.05, 1491.17) * mm, "end": v(0, 1489.08) * mm});
            skPoint(sketch, "E20.11.0.59", {"position": v(0, 1503.36) * mm});
            skLineSegment(sketch, "E20.12.0.59", {"start": v(7.14, 1517.65) * mm, "end": v(7.14, 1489.08) * mm, "construction": true});
            skLineSegment(sketch, "E20.15.0.59", {"start": v(-7.14, 1510.5) * mm, "end": v(-7.14, 1496.22) * mm});
            skSolve(sketch);
        }
        {
            var Q0;
            Q0 = qSketchRegion(id + "F2", true);
            extrude(context, id + "F3", {"entities" : qUnion([Q0]), "operationType" : NewBodyOperationType.REMOVE, "endBound" : BoundingType.SYMMETRIC, "oppositeDirection" : true, "depth" : 25.4 * mm});
        }
        {
            var Q0;
            Q0=makeQuery(id+"F1.opExtrude","SWEPT_BODY",BODY,{"disambiguationData":[OSD([sQuery(id+"F0.wireOp",EDGE,"E1"),sQuery(id+"F0.wireOp",EDGE,"E2"),sQuery(id+"F0.wireOp",EDGE,"E3"),sQuery(id+"F0.wireOp",EDGE,"E4"),sQuery(id+"F0.wireOp",EDGE,"E5.filletArc"),sQuery(id+"F0.wireOp",EDGE,"E6.filletArc"),sQuery(id+"F0.wireOp",EDGE,"E7.filletArc"),sQuery(id+"F0.wireOp",EDGE,"E8.0"),sQuery(id+"F0.wireOp",EDGE,"E8.1"),sQuery(id+"F0.wireOp",EDGE,"E8.2"),sQuery(id+"F0.wireOp",EDGE,"E8.3"),sQuery(id+"F0.wireOp",EDGE,"E8.4"),sQuery(id+"F0.wireOp",EDGE,"E8.5"),sQuery(id+"F0.wireOp",EDGE,"E8.6"),sQuery(id+"F0.wireOp",EDGE,"E9"),sQuery(id+"F0.wireOp",EDGE,"E10")])]});
            var Q1;
            Q1=qCreatedBy(makeId("Right.planeOp"),FACE);
            mirror(context, id + "F4", {"operationType" : NewBodyOperationType.ADD, "entities" : qUnion([Q0]), "mirrorPlane" : qUnion([Q1])});
        }
    });
